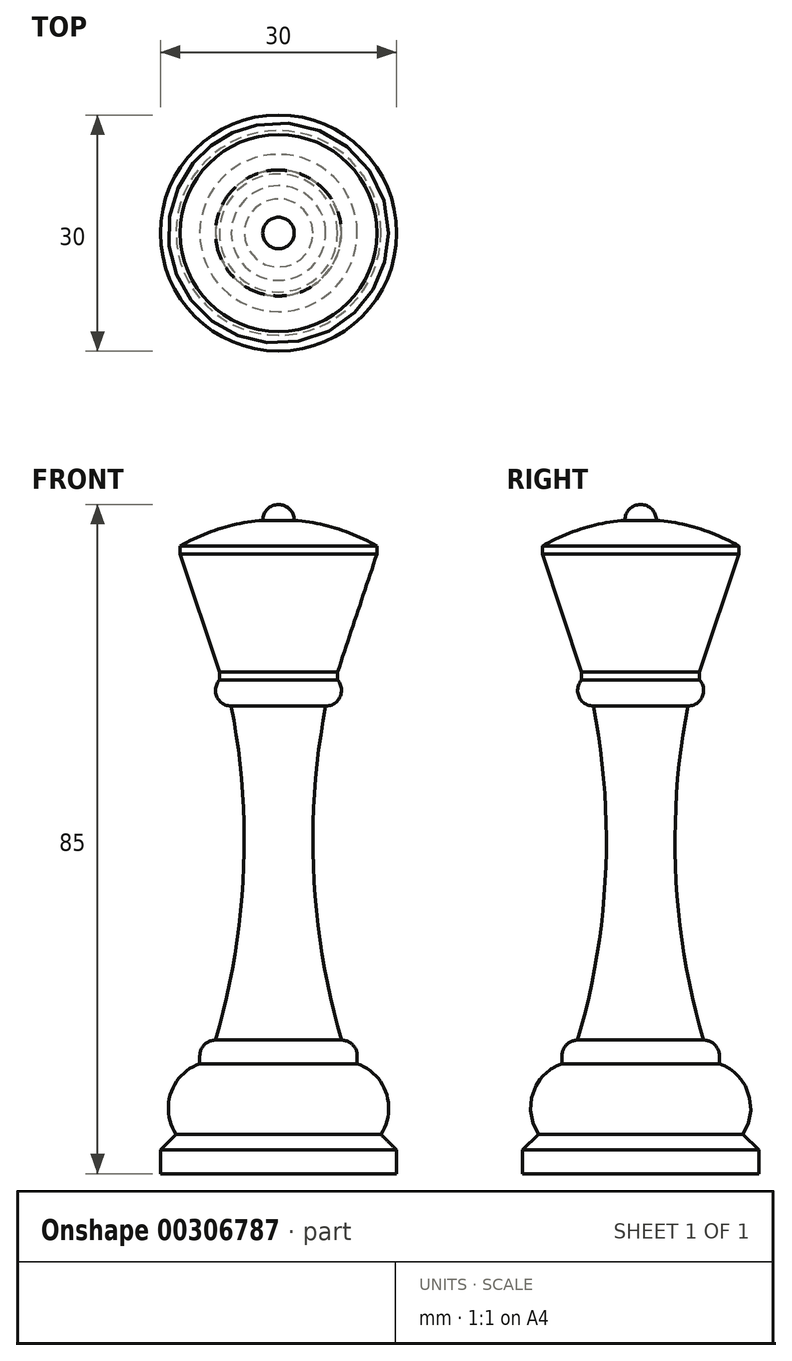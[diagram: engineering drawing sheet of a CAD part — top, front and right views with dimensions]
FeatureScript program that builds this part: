
annotation { "Feature Type Name" : "Feature", "Feature Type Description" : "" }
export const myFeature = defineFeature(function(context is Context, id is Id, definition is map)
    precondition{}
    {
        {
            var Q0;
            Q0=qCreatedBy(makeId("Front.planeOp"),FACE);
            var sketch = newSketch(context, id + "F0", { "sketchPlane" : qUnion([Q0])});
            skLineSegment(sketch, "E0", {"start": v(0, 0) * mm, "end": v(0, -85) * mm});
            skLineSegment(sketch, "E1", {"start": v(10, -71.03) * mm, "end": v(10, -70.03) * mm});
            skArc(sketch, "E2", {"start": v(10, -70.03) * mm, "mid": v(9.41, -68.62) * mm, "end": v(8, -68.03) * mm});
            skArc(sketch, "E3", {"start": v(6, -25.6) * mm, "mid": v(4.46, -46.93) * mm, "end": v(8, -68.03) * mm});
            skArc(sketch, "E4", {"start": v(6, -25.6) * mm, "mid": v(7.82, -24.42) * mm, "end": v(7.5, -22.27) * mm});
            skLineSegment(sketch, "E5", {"start": v(7.5, -22.27) * mm, "end": v(7.5, -21.27) * mm});
            skLineSegment(sketch, "E6", {"start": v(7.5, -21.27) * mm, "end": v(12.5, -6.27) * mm});
            skLineSegment(sketch, "E7", {"start": v(12.5, -6.27) * mm, "end": v(12.5, -5.27) * mm});
            skArc(sketch, "E8", {"start": v(12.5, -5.27) * mm, "mid": v(7.43, -3.05) * mm, "end": v(2, -2) * mm});
            skLineSegment(sketch, "E9", {"start": v(0, -85) * mm, "end": v(15, -85) * mm});
            skLineSegment(sketch, "E10", {"start": v(15, -85) * mm, "end": v(15, -82) * mm});
            skLineSegment(sketch, "E11", {"start": v(15, -82) * mm, "end": v(13, -80) * mm});
            skArc(sketch, "E12", {"start": v(13, -80) * mm, "mid": v(13.69, -74.78) * mm, "end": v(10, -71.03) * mm});
            skArc(sketch, "E13", {"start": v(2, -2) * mm, "mid": v(1.41, -0.59) * mm, "end": v(0, 0) * mm});
            skSolve(sketch);
        }
        {
            var Q0;
            Q0=makeQuery(id+"F0.imprint","IMPRINT",FACE,{"disambiguationData":[TD([[makeQuery(id+"F0.imprint","IMPRINT",EDGE,{"derivedFrom":sQuery(id+"F0.wireOp",EDGE,"E0")}),1.0]])]});
            var Q1;
            Q1=sQuery(id+"F0.wireOp",EDGE,"E0");
            revolve(context, id + "F1", {"entities" : qUnion([Q0]), "axis" : qUnion([Q1]), "revolveType" : RevolveType.FULL});
        }
    });
